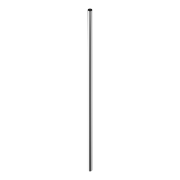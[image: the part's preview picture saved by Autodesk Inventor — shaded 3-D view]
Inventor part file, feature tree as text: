
AUTODESK INVENTOR PART (.ipt)
format: ipt  version: 2019.4 (Build 234330000, 330)  size: 69,632 bytes
history: native  units: in
note: dims shown in document units (in); Inventor stores cm internally (conversion verified against a paired STEP export)
features: extrude x1, sketch x1
ambient origin geometry x8: Origin, YZ Plane, XZ Plane, XY Plane, X Axis, Y Axis, Z Axis, Center Point
bodies: Solid1 (feature_tree)
feature tree (2):
  extrude  "Extrusion1"  Depth=9.8425in TaperAngle=0.0deg
  sketch  "Sketch1"  dims[d0=0.2362in d1=9.8425in d2=0.0in]
